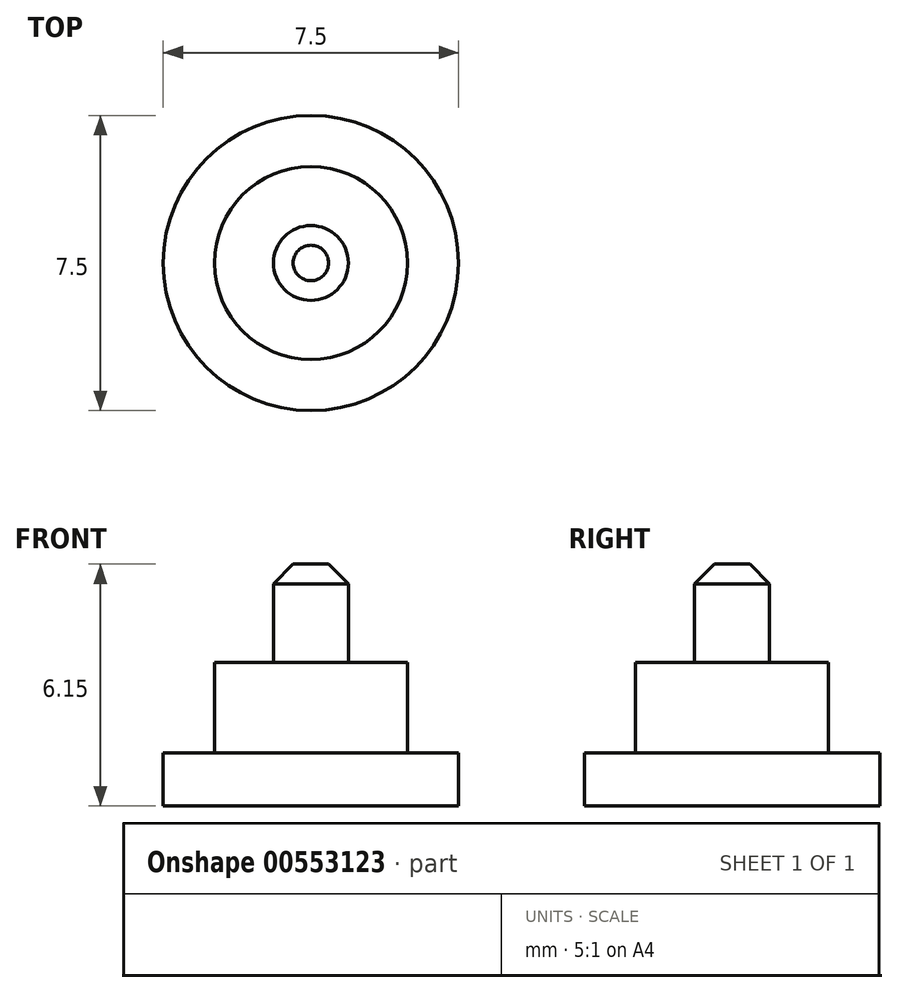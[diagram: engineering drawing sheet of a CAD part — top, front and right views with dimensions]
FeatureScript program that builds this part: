
annotation { "Feature Type Name" : "Feature", "Feature Type Description" : "" }
export const myFeature = defineFeature(function(context is Context, id is Id, definition is map)
    precondition{}
    {
        {
            var Q0;
            Q0=qCreatedBy(makeId("Top.planeOp"),FACE);
            var sketch = newSketch(context, id + "F0", { "sketchPlane" : qUnion([Q0])});
            skCircle(sketch, "E0", {"center": v(0, 0) * mm, "radius": 3.75 * mm});
            skSolve(sketch);
        }
        {
            var Q0;
            Q0 = qSketchRegion(id + "F0", true);
            extrude(context, id + "F1", {"entities" : qUnion([Q0]), "depth" : 1.35 * mm, "offsetDistance" : 25 * mm});
        }
        {
            var Q0;
            Q0=makeQuery(id+"F1.opExtrude","CAP_FACE",FACE,{"disambiguationData":[OSD([sQuery(id+"F0.wireOp",EDGE,"E0")])],"isStart":false});
            var sketch = newSketch(context, id + "F2", { "sketchPlane" : qUnion([Q0])});
            skCircle(sketch, "E1", {"center": v(0, 0) * mm, "radius": 2.45 * mm});
            skSolve(sketch);
        }
        {
            var Q0;
            Q0 = qSketchRegion(id + "F2", true);
            extrude(context, id + "F3", {"entities" : qUnion([Q0]), "operationType" : NewBodyOperationType.ADD, "depth" : 2.3 * mm, "offsetDistance" : 25 * mm});
        }
        {
            var Q0;
            Q0=makeQuery(id+"F3.opExtrude","CAP_FACE",FACE,{"disambiguationData":[OSD([sQuery(id+"F2.wireOp",EDGE,"E1")])],"isStart":false});
            var sketch = newSketch(context, id + "F4", { "sketchPlane" : qUnion([Q0])});
            skCircle(sketch, "E2", {"center": v(0, 0) * mm, "radius": 0.95 * mm});
            skSolve(sketch);
        }
        {
            var Q0;
            Q0 = qSketchRegion(id + "F4", true);
            extrude(context, id + "F5", {"entities" : qUnion([Q0]), "operationType" : NewBodyOperationType.ADD, "depth" : 2.5 * mm, "offsetDistance" : 25 * mm});
        }
        {
            var Q0;
            Q0=makeQuery(id+"F5.opExtrude","CAP_EDGE",EDGE,{"disambiguationData":[OSD([sQuery(id+"F4.wireOp",EDGE,"E2")])],"isStart":false});
            chamfer(context, id + "F6", {"entities" : qUnion([Q0]), "width" : 0.5 * mm, "tangentPropagation" : true});
        }
    });
